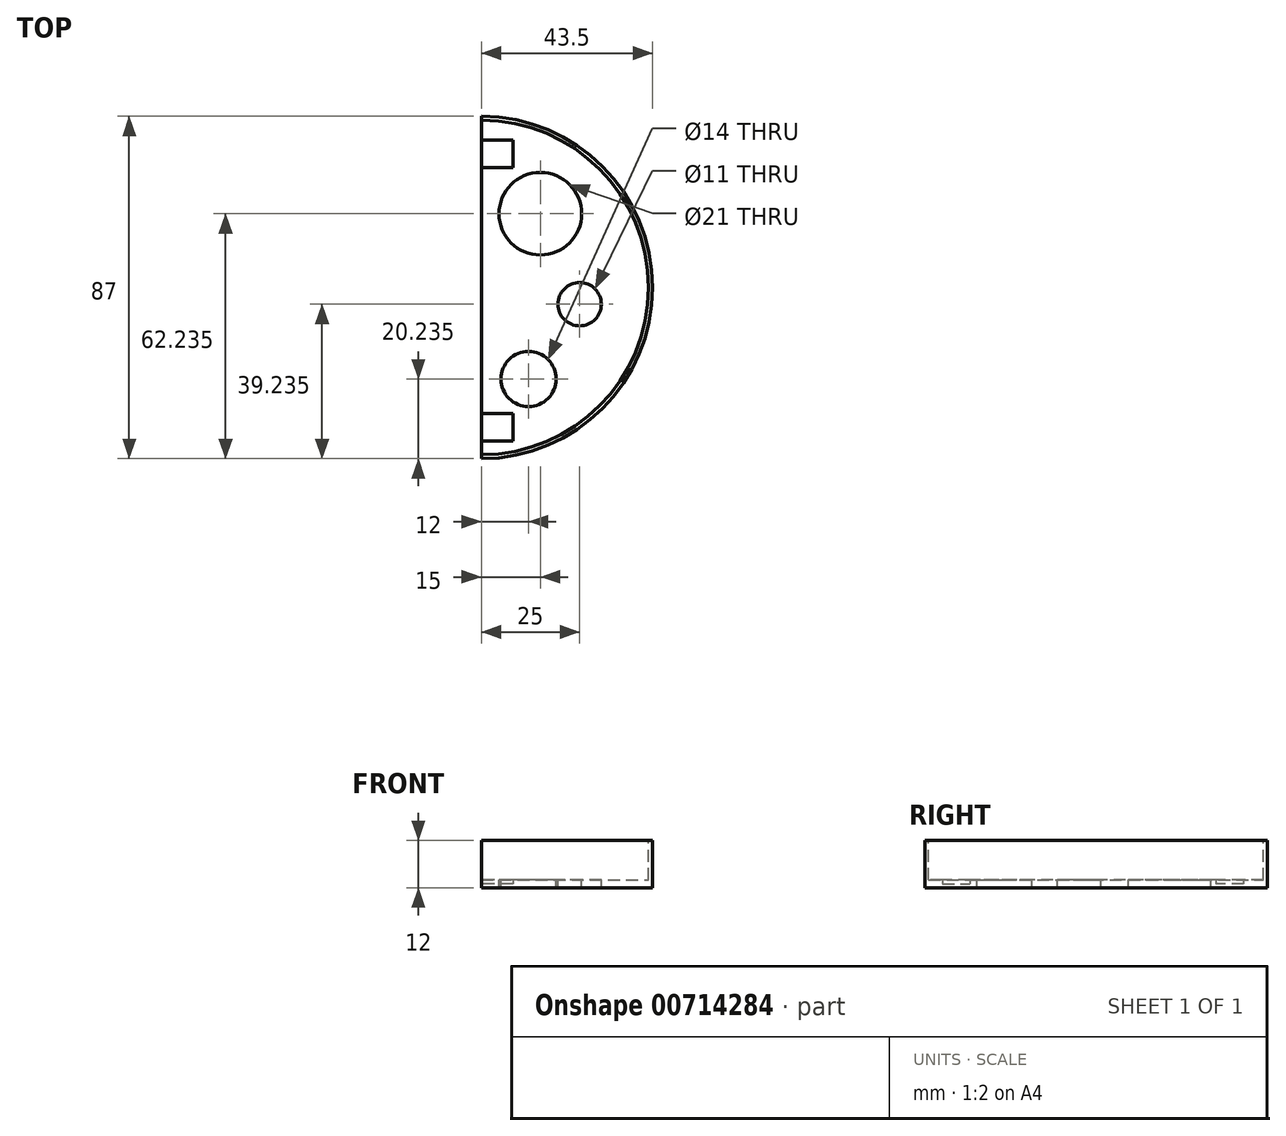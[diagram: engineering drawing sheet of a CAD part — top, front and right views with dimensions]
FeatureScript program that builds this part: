
annotation { "Feature Type Name" : "Feature", "Feature Type Description" : "" }
export const myFeature = defineFeature(function(context is Context, id is Id, definition is map)
    precondition{}
    {
        {
            var Q0;
            Q0=qCreatedBy(makeId("Top.planeOp"),FACE);
            var sketch = newSketch(context, id + "F0", { "sketchPlane" : qUnion([Q0])});
            skArc(sketch, "E0", {"start": v(0, -43.5) * mm, "mid": v(43.5, 0) * mm, "end": v(0, 43.5) * mm});
            skPoint(sketch, "E1", {"position": v(0, 43.5) * mm});
            skPoint(sketch, "E2", {"position": v(0, -43.5) * mm});
            skLineSegment(sketch, "E3", {"start": v(0, 43.5) * mm, "end": v(0, -43.5) * mm});
            skSolve(sketch);
        }
        {
            var Q0;
            Q0=qSketchRegion(id+"F0",true);
            extrude(context, id + "F1", {"entities" : qUnion([Q0]), "depth" : 12 * mm, "offsetDistance" : 25 * mm});
        }
        {
            var Q0;
            Q0=makeQuery(id+"F1.opExtrude","CAP_FACE",FACE,{"disambiguationData":[OSD([sQuery(id+"F0.wireOp",EDGE,"E0")])],"isStart":false});
            var sketch = newSketch(context, id + "F2", { "sketchPlane" : qUnion([Q0])});
            skCircle(sketch, "E4", {"center": v(0, 0) * mm, "radius": 42.5 * mm});
            skSolve(sketch);
        }
        {
            var Q0;
            Q0=qSketchRegion(id+"F2",true);
            extrude(context, id + "F3", {"entities" : qUnion([Q0]), "operationType" : NewBodyOperationType.REMOVE, "oppositeDirection" : true, "depth" : 10 * mm, "offsetDistance" : 25 * mm});
        }
        {
            var Q0;
            Q0=makeQuery(id+"F3.boolean.opBoolean","COPY",FACE,{"derivedFrom":makeQuery(id+"F3.opExtrude","CAP_FACE",FACE,{"disambiguationData":[OSD([sQuery(id+"F2.wireOp",EDGE,"E4")])],"isStart":false})});
            var sketch = newSketch(context, id + "F4", { "sketchPlane" : qUnion([Q0])});
            skCircle(sketch, "E5", {"center": v(-15, 18.73) * mm, "radius": 10.5 * mm});
            skCircle(sketch, "E6", {"center": v(-25, -4.27) * mm, "radius": 5.5 * mm});
            skCircle(sketch, "E7", {"center": v(-12, -23.27) * mm, "radius": 7 * mm});
            skCircle(sketch, "E8.MirrorC", {"center": v(15, 18.73) * mm, "radius": 10.5 * mm});
            skCircle(sketch, "E9.MirrorC", {"center": v(25, -4.27) * mm, "radius": 5.5 * mm});
            skCircle(sketch, "E10.MirrorC", {"center": v(12, -23.27) * mm, "radius": 7 * mm});
            skSolve(sketch);
        }
        {
            var Q0;
            Q0=qSketchRegion(id+"F4",true);
            extrude(context, id + "F5", {"entities" : qUnion([Q0]), "operationType" : NewBodyOperationType.REMOVE, "endBound" : BoundingType.THROUGH_ALL, "oppositeDirection" : true, "depth" : 25 * mm, "offsetDistance" : 25 * mm});
        }
        {
            var Q0;
            Q0=makeQuery(id+"F1.opExtrude","SWEPT_FACE",FACE,{"disambiguationData":[OSD([sQuery(id+"F0.wireOp",EDGE,"E3")])]});
            var sketch = newSketch(context, id + "F6", { "sketchPlane" : qUnion([Q0])});
            skLineSegment(sketch, "E11.bottom", {"start": v(-37.5, 2) * mm, "end": v(-30.5, 2) * mm});
            skLineSegment(sketch, "E11.top", {"start": v(-37.5, 1) * mm, "end": v(-30.5, 1) * mm});
            skLineSegment(sketch, "E11.left", {"start": v(-37.5, 2) * mm, "end": v(-37.5, 1) * mm});
            skLineSegment(sketch, "E11.right", {"start": v(-30.5, 2) * mm, "end": v(-30.5, 1) * mm});
            skLineSegment(sketch, "E12.bottom", {"start": v(39, 2) * mm, "end": v(32, 2) * mm});
            skLineSegment(sketch, "E12.top", {"start": v(39, 1) * mm, "end": v(32, 1) * mm});
            skLineSegment(sketch, "E12.left", {"start": v(39, 2) * mm, "end": v(39, 1) * mm});
            skLineSegment(sketch, "E12.right", {"start": v(32, 2) * mm, "end": v(32, 1) * mm});
            skSolve(sketch);
        }
        {
            var Q0;
            Q0 = qSketchRegion(id + "F6", true);
            extrude(context, id + "F7", {"entities" : qUnion([Q0]), "operationType" : NewBodyOperationType.REMOVE, "oppositeDirection" : true, "depth" : 8 * mm, "offsetDistance" : 25 * mm});
        }
    });
